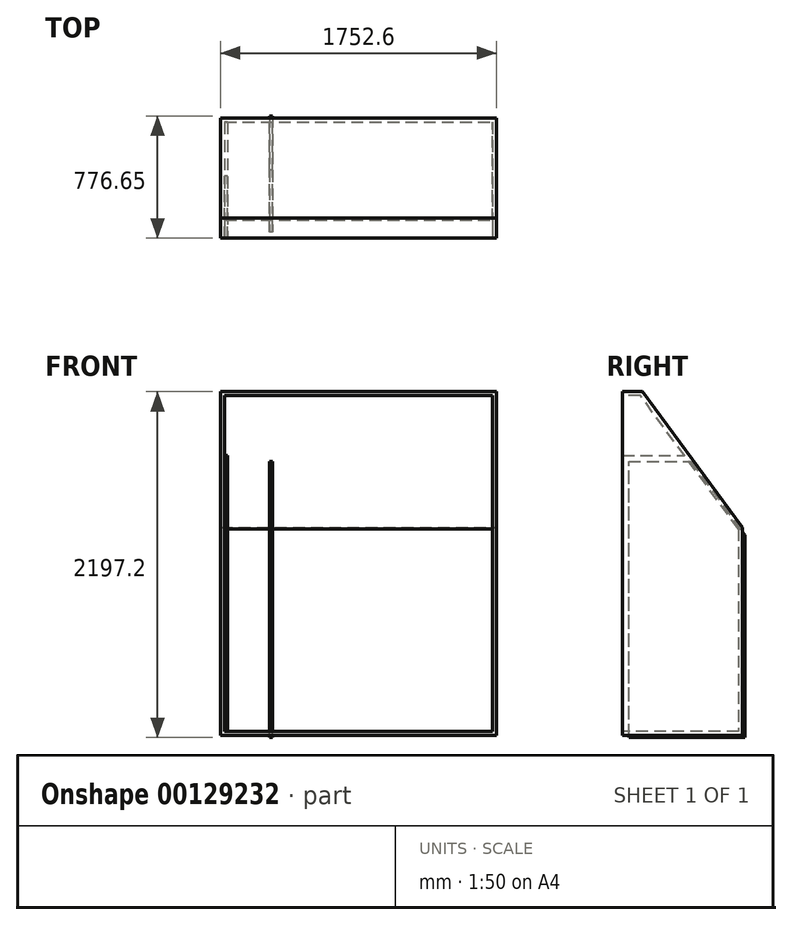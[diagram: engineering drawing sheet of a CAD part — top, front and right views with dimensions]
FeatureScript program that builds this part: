
annotation { "Feature Type Name" : "Feature", "Feature Type Description" : "" }
export const myFeature = defineFeature(function(context is Context, id is Id, definition is map)
    precondition{}
    {
        {
            var Q0;
            Q0=qCreatedBy(makeId("Front.planeOp"),FACE);
            var sketch = newSketch(context, id + "F0", { "sketchPlane" : qUnion([Q0])});
            skLineSegment(sketch, "E0.bottom", {"start": v(-987.3, 1120) * mm, "end": v(765.3, 1120) * mm});
            skLineSegment(sketch, "E0.left", {"start": v(-987.3, 1120) * mm, "end": v(-987.3, -1064.4) * mm});
            skLineSegment(sketch, "E0.right", {"start": v(765.3, 1120) * mm, "end": v(765.3, -1064.4) * mm});
            skLineSegment(sketch, "E1", {"start": v(-987.3, -1064.4) * mm, "end": v(765.3, -1064.4) * mm});
            skSolve(sketch);
        }
        {
            var Q0;
            Q0=makeQuery(id+"F0.imprint","IMPRINT",FACE,{"disambiguationData":[TD([[makeQuery(id+"F0.imprint","IMPRINT",EDGE,{"derivedFrom":sQuery(id+"F0.wireOp",EDGE,"E0.bottom")}),-1.0]])]});
            extrude(context, id + "F1", {"entities" : qUnion([Q0]), "oppositeDirection" : true, "depth" : 762 * mm});
        }
        {
            var Q0;
            Q0=makeQuery(id+"F1.opExtrude","CAP_EDGE",EDGE,{"disambiguationData":[OSD([sQuery(id+"F0.wireOp",EDGE,"E0.bottom")])],"isStart":false});
            chamfer(context, id + "F2", {"entities" : qUnion([Q0]), "chamferType" : ChamferType.TWO_OFFSETS, "width1" : 863.6 * mm, "oppositeDirection" : false, "width2" : 635 * mm});
        }
        {
            var Q0;
            Q0=makeQuery(id+"F1.opExtrude","CAP_FACE",FACE,{"disambiguationData":[OSD([sQuery(id+"F0.wireOp",EDGE,"E0.bottom"),sQuery(id+"F0.wireOp",EDGE,"E0.left"),sQuery(id+"F0.wireOp",EDGE,"E0.right"),sQuery(id+"F0.wireOp",EDGE,"E1")])],"isStart":true});
            shell(context, id + "F3", {"entities" : qUnion([Q0]), "thickness" : 25.4 * mm});
        }
        {
            var Q0;
            Q0=makeQuery(id+"F3.opShell","OFFSET_FACE",FACE,{"disambiguationData":[OSD([sQuery(id+"F0.wireOp",EDGE,"E0.left")])]});
            var sketch = newSketch(context, id + "F4", { "sketchPlane" : qUnion([Q0])});
            skLineSegment(sketch, "E2", {"start": v(736.6, 248.08) * mm, "end": v(736.6, -1039) * mm});
            skLineSegment(sketch, "E3", {"start": v(736.6, -1039) * mm, "end": v(0, -1039) * mm});
            skLineSegment(sketch, "E4", {"start": v(0, -1039) * mm, "end": v(0, 714.68) * mm});
            skLineSegment(sketch, "E5", {"start": v(0, 714.68) * mm, "end": v(393.51, 714.68) * mm});
            skLineSegment(sketch, "E6", {"start": v(393.51, 714.68) * mm, "end": v(736.6, 248.08) * mm});
            skSolve(sketch);
        }
        {
            var Q0;
            Q0=makeQuery(id+"F4.imprint","IMPRINT",FACE,{"disambiguationData":[TD([[makeQuery(id+"F4.imprint","IMPRINT",EDGE,{"derivedFrom":sQuery(id+"F4.wireOp",EDGE,"E2")}),-1.0]])]});
            extrude(context, id + "F5", {"entities" : qUnion([Q0]), "depth" : 19.05 * mm});
        }
        {
            var Q0;
            Q0=makeQuery(id+"F5.opExtrude","CAP_FACE",FACE,{"disambiguationData":[OSD([sQuery(id+"F4.wireOp",EDGE,"lTaifl4j-A9yD-Cv9i-GrLW-2gMndGf3MAi3"),sQuery(id+"F4.wireOp",EDGE,"nNGVrXGi-gYdG-rvpL-Ag4s-2J8lZ2PBcz4k"),sQuery(id+"F4.wireOp",EDGE,"E2"),sQuery(id+"F4.wireOp",EDGE,"E3"),sQuery(id+"F4.wireOp",EDGE,"cgE2ChD7-IcWb-iTRY-Ui7x-7Ei4IkhRnzsR")])],"isStart":false});
            cPlane(context, id + "F6", {"entities" : qUnion([Q0]), "cplaneType" : CPlaneType.OFFSET, "offset" : 266.7 * mm, "width" : 152.4 * mm, "height" : 152.4 * mm});
        }
        {
            var Q0;
            Q0=qCreatedBy(id+"F6.planeOp",FACE);
            var sketch = newSketch(context, id + "F7", { "sketchPlane" : qUnion([Q0])});
            skLineSegment(sketch, "E7", {"start": v(776.65, 209.88) * mm, "end": v(776.65, -1077.19) * mm});
            skLineSegment(sketch, "E8", {"start": v(776.65, -1077.19) * mm, "end": v(40.05, -1077.19) * mm});
            skLineSegment(sketch, "E9", {"start": v(40.05, -1077.19) * mm, "end": v(40.05, 676.48) * mm});
            skLineSegment(sketch, "E10", {"start": v(40.05, 676.48) * mm, "end": v(433.56, 676.48) * mm});
            skLineSegment(sketch, "E11", {"start": v(433.56, 676.48) * mm, "end": v(776.65, 209.88) * mm});
            skSolve(sketch);
        }
        {
            var Q0;
            Q0 = qSketchRegion(id + "F7", true);
            var Q1;
            Q1=sQuery(id+"F7.wireOp",EDGE,"E7");
            var Q2;
            Q2=sQuery(id+"F7.wireOp",EDGE,"E8");
            var Q3;
            Q3=sQuery(id+"F7.wireOp",EDGE,"E10");
            var Q4;
            Q4=sQuery(id+"F7.wireOp",EDGE,"E11");
            var Q5;
            Q5=sQuery(id+"F7.wireOp",EDGE,"E9");
            extrude(context, id + "F8", {"entities" : qUnion([Q0]), "surfaceEntities" : qUnion([Q1, Q2, Q3, Q4, Q5]), "depth" : 19.05 * mm});
        }
    });
